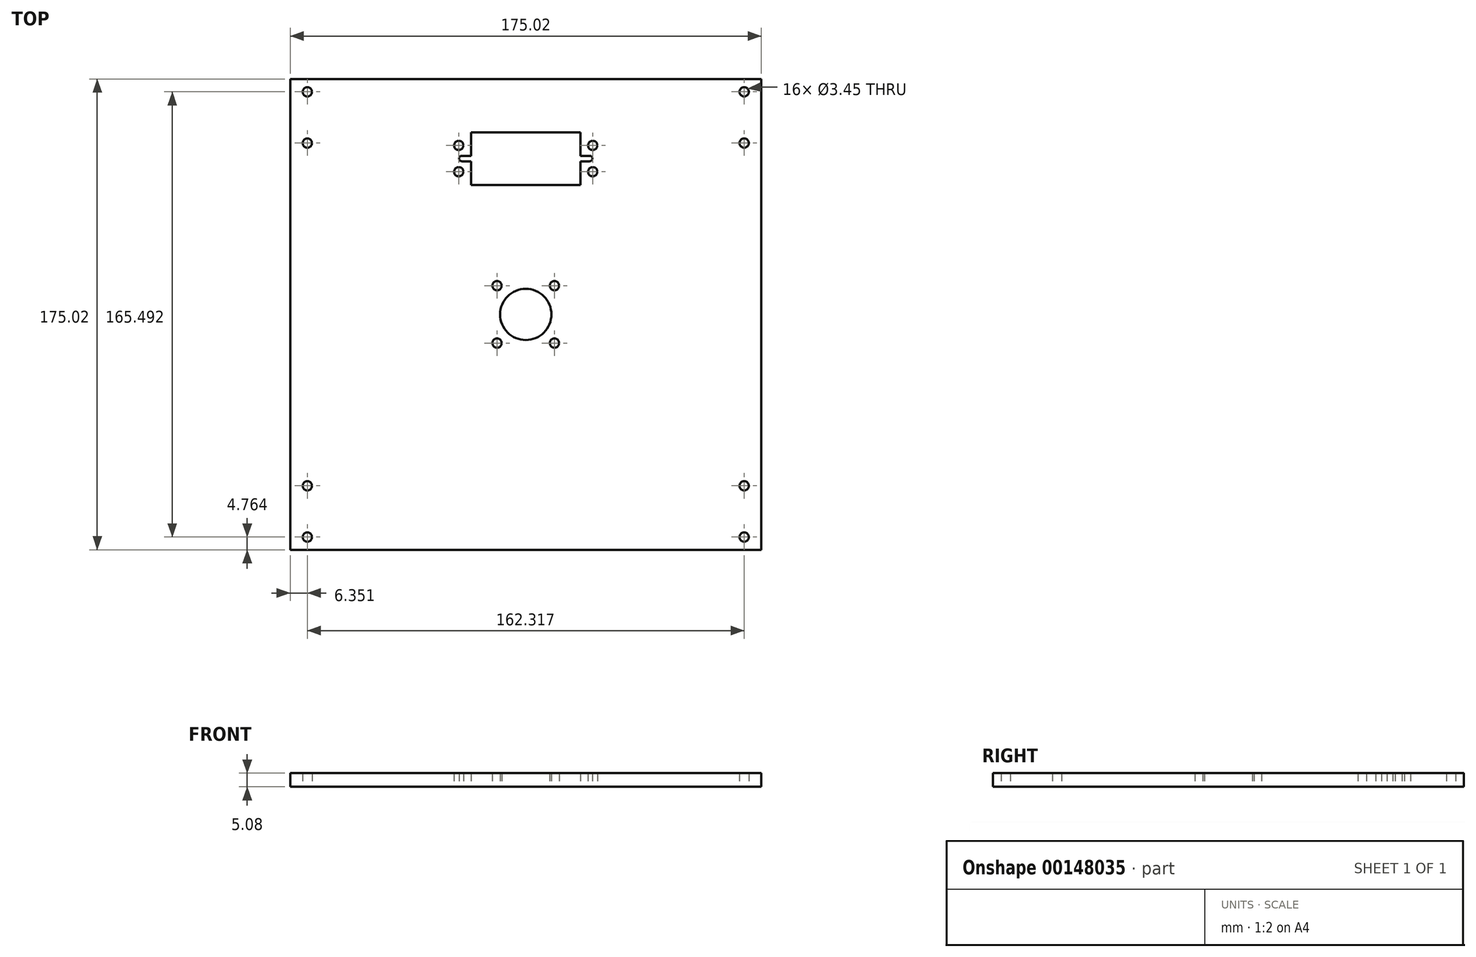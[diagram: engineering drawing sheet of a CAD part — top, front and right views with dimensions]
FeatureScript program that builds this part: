
annotation { "Feature Type Name" : "Feature", "Feature Type Description" : "" }
export const myFeature = defineFeature(function(context is Context, id is Id, definition is map)
    precondition{}
    {
        {
            var Q0;
            Q0=qCreatedBy(makeId("Top.planeOp"),FACE);
            var sketch = newSketch(context, id + "F0", { "sketchPlane" : qUnion([Q0])});
            skLineSegment(sketch, "E0.bottom", {"start": v(-10.66, 10.66) * mm, "end": v(10.66, 10.66) * mm, "construction": true});
            skLineSegment(sketch, "E0.top", {"start": v(-10.66, -10.66) * mm, "end": v(10.66, -10.66) * mm, "construction": true});
            skLineSegment(sketch, "E0.left", {"start": v(-10.66, 10.66) * mm, "end": v(-10.66, -10.66) * mm, "construction": true});
            skLineSegment(sketch, "E0.right", {"start": v(10.66, 10.66) * mm, "end": v(10.66, -10.66) * mm, "construction": true});
            skPoint(sketch, "E0.middle", {"position": v(0, 0) * mm});
            skCircle(sketch, "E1", {"center": v(0, 0) * mm, "radius": 11.11 * mm, "construction": true});
            skCircle(sketch, "E2", {"center": v(-10.66, 10.66) * mm, "radius": 3.97 * mm, "construction": true});
            skCircle(sketch, "E3", {"center": v(-10.66, 10.66) * mm, "radius": 1.73 * mm});
            skCircle(sketch, "E4", {"center": v(10.66, 10.66) * mm, "radius": 1.73 * mm});
            skCircle(sketch, "E5", {"center": v(10.66, -10.66) * mm, "radius": 1.73 * mm});
            skCircle(sketch, "E6", {"center": v(-10.66, -10.66) * mm, "radius": 1.73 * mm});
            skLineSegment(sketch, "E7", {"start": v(0, 0) * mm, "end": v(0, 0) * mm});
            skLineSegment(sketch, "E8.bottom", {"start": v(-87.5, 87.5) * mm, "end": v(87.5, 87.5) * mm});
            skLineSegment(sketch, "E8.top", {"start": v(-87.5, -87.5) * mm, "end": v(87.5, -87.5) * mm});
            skLineSegment(sketch, "E8.left", {"start": v(-87.5, 87.5) * mm, "end": v(-87.5, -87.5) * mm});
            skLineSegment(sketch, "E8.right", {"start": v(87.5, 87.5) * mm, "end": v(87.5, -87.5) * mm});
            skLineSegment(sketch, "E9", {"start": v(-87.5, 82.75) * mm, "end": v(-81.16, 82.75) * mm, "construction": true});
            skLineSegment(sketch, "E10", {"start": v(-81.16, 82.75) * mm, "end": v(-81.16, 87.5) * mm, "construction": true});
            skLineSegment(sketch, "E11", {"start": v(-81.16, -87.5) * mm, "end": v(-81.16, -82.75) * mm, "construction": true});
            skLineSegment(sketch, "E12", {"start": v(-81.16, -82.75) * mm, "end": v(-81.16, -63.7) * mm, "construction": true});
            skLineSegment(sketch, "E13", {"start": v(81.16, 87.5) * mm, "end": v(81.16, 82.75) * mm, "construction": true});
            skLineSegment(sketch, "E14", {"start": v(81.16, 82.75) * mm, "end": v(87.5, 82.75) * mm, "construction": true});
            skLineSegment(sketch, "E15", {"start": v(81.16, 82.75) * mm, "end": v(81.16, 63.7) * mm, "construction": true});
            skLineSegment(sketch, "E16", {"start": v(-81.16, 82.75) * mm, "end": v(-81.16, 63.7) * mm, "construction": true});
            skLineSegment(sketch, "E17", {"start": v(81.16, -87.5) * mm, "end": v(81.16, -82.75) * mm, "construction": true});
            skLineSegment(sketch, "E18", {"start": v(81.16, -82.75) * mm, "end": v(81.16, -63.7) * mm, "construction": true});
            skCircle(sketch, "E19", {"center": v(-81.16, 82.75) * mm, "radius": 1.73 * mm});
            skCircle(sketch, "E20", {"center": v(-81.16, 63.7) * mm, "radius": 1.73 * mm});
            skCircle(sketch, "E21", {"center": v(-81.16, -63.7) * mm, "radius": 1.73 * mm});
            skCircle(sketch, "E22", {"center": v(-81.16, -82.75) * mm, "radius": 1.73 * mm});
            skCircle(sketch, "E23", {"center": v(81.16, -82.75) * mm, "radius": 1.73 * mm});
            skCircle(sketch, "E24", {"center": v(81.16, -63.7) * mm, "radius": 1.73 * mm});
            skCircle(sketch, "E25", {"center": v(81.16, 63.7) * mm, "radius": 1.73 * mm});
            skCircle(sketch, "E26", {"center": v(81.16, 82.75) * mm, "radius": 1.73 * mm});
            skLineSegment(sketch, "E27", {"start": v(0, 0) * mm, "end": v(0, 48.16) * mm, "construction": true});
            skLineSegment(sketch, "E28", {"start": v(0, 48.16) * mm, "end": v(0, 67.72) * mm, "construction": true});
            skLineSegment(sketch, "E29", {"start": v(-20.32, 67.72) * mm, "end": v(20.32, 67.72) * mm});
            skLineSegment(sketch, "E30", {"start": v(-20.32, 48.16) * mm, "end": v(20.32, 48.16) * mm});
            skLineSegment(sketch, "E31", {"start": v(-20.32, 67.72) * mm, "end": v(-20.32, 58.96) * mm});
            skLineSegment(sketch, "E32", {"start": v(-20.32, 48.16) * mm, "end": v(-20.32, 56.92) * mm});
            skLineSegment(sketch, "E33", {"start": v(20.32, 48.16) * mm, "end": v(20.32, 56.92) * mm});
            skLineSegment(sketch, "E34", {"start": v(20.32, 67.72) * mm, "end": v(20.32, 58.96) * mm});
            skLineSegment(sketch, "E35.bottom", {"start": v(20.32, 58.96) * mm, "end": v(23.75, 58.96) * mm});
            skLineSegment(sketch, "E35.top", {"start": v(20.32, 56.92) * mm, "end": v(23.75, 56.92) * mm});
            skLineSegment(sketch, "E35.left", {"start": v(20.32, 58.96) * mm, "end": v(20.32, 56.92) * mm, "construction": true});
            skLineSegment(sketch, "E35.right", {"start": v(23.75, 58.96) * mm, "end": v(23.75, 56.92) * mm, "construction": true});
            skLineSegment(sketch, "E36.bottom", {"start": v(-20.32, 58.96) * mm, "end": v(-23.75, 58.96) * mm});
            skLineSegment(sketch, "E36.top", {"start": v(-20.32, 56.92) * mm, "end": v(-23.75, 56.92) * mm});
            skLineSegment(sketch, "E36.left", {"start": v(-20.32, 58.96) * mm, "end": v(-20.32, 56.92) * mm, "construction": true});
            skLineSegment(sketch, "E36.right", {"start": v(-23.75, 58.96) * mm, "end": v(-23.75, 56.92) * mm, "construction": true});
            skLineSegment(sketch, "E37.bottom", {"start": v(-24.9, 62.83) * mm, "end": v(24.9, 62.83) * mm, "construction": true});
            skLineSegment(sketch, "E37.top", {"start": v(-24.9, 53.05) * mm, "end": v(24.9, 53.05) * mm, "construction": true});
            skLineSegment(sketch, "E37.left", {"start": v(-24.9, 62.83) * mm, "end": v(-24.9, 53.05) * mm, "construction": true});
            skLineSegment(sketch, "E37.right", {"start": v(24.9, 62.83) * mm, "end": v(24.9, 53.05) * mm, "construction": true});
            skPoint(sketch, "E37.middle", {"position": v(0, 57.94) * mm});
            skArc(sketch, "E38", {"start": v(-23.75, 58.96) * mm, "mid": v(-24.77, 57.94) * mm, "end": v(-23.75, 56.92) * mm});
            skArc(sketch, "E39", {"start": v(23.75, 56.92) * mm, "mid": v(24.77, 57.94) * mm, "end": v(23.75, 58.96) * mm});
            skCircle(sketch, "E40", {"center": v(-24.9, 62.83) * mm, "radius": 1.73 * mm});
            skCircle(sketch, "E41", {"center": v(-24.9, 53.05) * mm, "radius": 1.73 * mm});
            skCircle(sketch, "E42", {"center": v(24.9, 53.05) * mm, "radius": 1.73 * mm});
            skCircle(sketch, "E43", {"center": v(24.9, 62.83) * mm, "radius": 1.73 * mm});
            skCircle(sketch, "E44", {"center": v(0, 0) * mm, "radius": 9.53 * mm});
            skSolve(sketch);
        }
        {
            var Q0;
            Q0=qSketchRegion(id+"F0",true);
            extrude(context, id + "F1", {"entities" : qUnion([Q0]), "depth" : 5.08 * mm});
        }
    });
